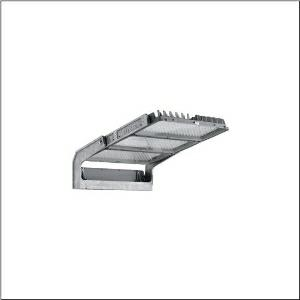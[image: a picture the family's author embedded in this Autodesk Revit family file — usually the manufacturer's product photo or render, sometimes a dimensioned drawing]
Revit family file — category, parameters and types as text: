
# Revit family: floodlight_fl_11_maxi_pro___rs07_5xa779128k02fb_ed38
name_source: partatom
category: Lighting Fixtures
units: mm (PartAtom-declared; Revit-internal decimal feet)

## family parameters
Cut with Voids When Loaded = No
Host = Face
Light Source = No
Part Type = Normal
Room Calculation Point = No
Round Connector Dimension = Use Diameter
Shared = No

## types (1)
- --- (1 x LED, 157630 lm, 1368.3 W, 5700K)
    Apparent Load = 1368 VA
    CIE Flux Codes = 80 93 99 100 99
    Color Rendering = 80
    Color Temperature = 5700K
    Default Elevation = 1800 mm
    Description = Floodlight FL 11  maxi  pro floodlight; light control with lens of PMMA; cover panel of toughened safety glass, transparent; light distribution: RS07, rotationally symmetric direct distribution, LEDcolour temperature: 5700K, rated luminous flux: 157.630lm, colour rendering: CRI > 80, light colour: 857; luminous efficacy: 115lm/W; brightness control: DALI 2; with terminal, 5-pole, max. 2.5mm², mains connection: 220..240V/380..400V AC, 50/60Hz, surge voltage resistance: line to ground: 10kV, service life up to 100,000h L90. Typical operating time: 1000h per year, ECG replaceable separately, LED unit replaceable without ESD environment, dustproof LED module, dimming range 10..100%; 1368W floodlight with 3x LED unit of diecast aluminium, coated grey; length: 1.003mm / width: 651mm / height: 338mm; mounting bracket, of diecast aluminium, uncoated, natural, protection rating (complete): IP66; insulation class (complete): insulation class I (protective earthing); certification: CE, ENEC, VDE; ball protection: ball impact resistant, only for outdoor installations in the designated locations, permissible operating ambient temperature: -45..+55°C, permissible storage temperature: -40..+85°Cpackaging unit: 1 piece

Light Distribution: RS07
    Height = 320 mm
    Lamp = 1 x LED
    Lamp Light Flux = 157630 lm
    Lamp Power = 1368.3 W
    Lamp count = 1
    Length = 1002 mm
    Luminous efficacy = 115 lm/W
    Manufacturer = Siteco
    ModVariant = No
    Model = 5XA779128K02FB
    Mounting Place = Ceiling
    Mounting Type = Surface mounted
    Number of Poles = 1
    OnlyDefault = Yes
    Power Factor = 1
    Product Name = Floodlight FL 11 maxi pro | RS07
    Product group = floodlight | ceiling mounted
    ProductGroupID = 301
    Protection Class = Protection class I
    Protection Degree = IP 66
    RLX_Detail_Level = 1
    RLX_Emergency_Light_Flux = 0 lm
    RLX_Emergency_Type = 0
    RLX_Emergency_Type_DB = No
    RlxData = <blob elided: 40401 chars, md5=b89f414e>
    Socket = socket
    Standby Power = 0 W
    System Light Flux = 157630 lm
    System Power = 1368 W
    Type Comments = factory setting: luminous flux: 100 % | dim-lin: 254 | 935 mA
    Type Image = l_1356210.jpg
    URL = http://relux.com
    VarID = @adj_023374
    Voltage = 0 V
    Weight = 0.00 kg
    Width = 655 mm

## geometry (parser evidence)
native form markers: Blend x4, Sweep x15
no freeform markers — native parametric forms only
